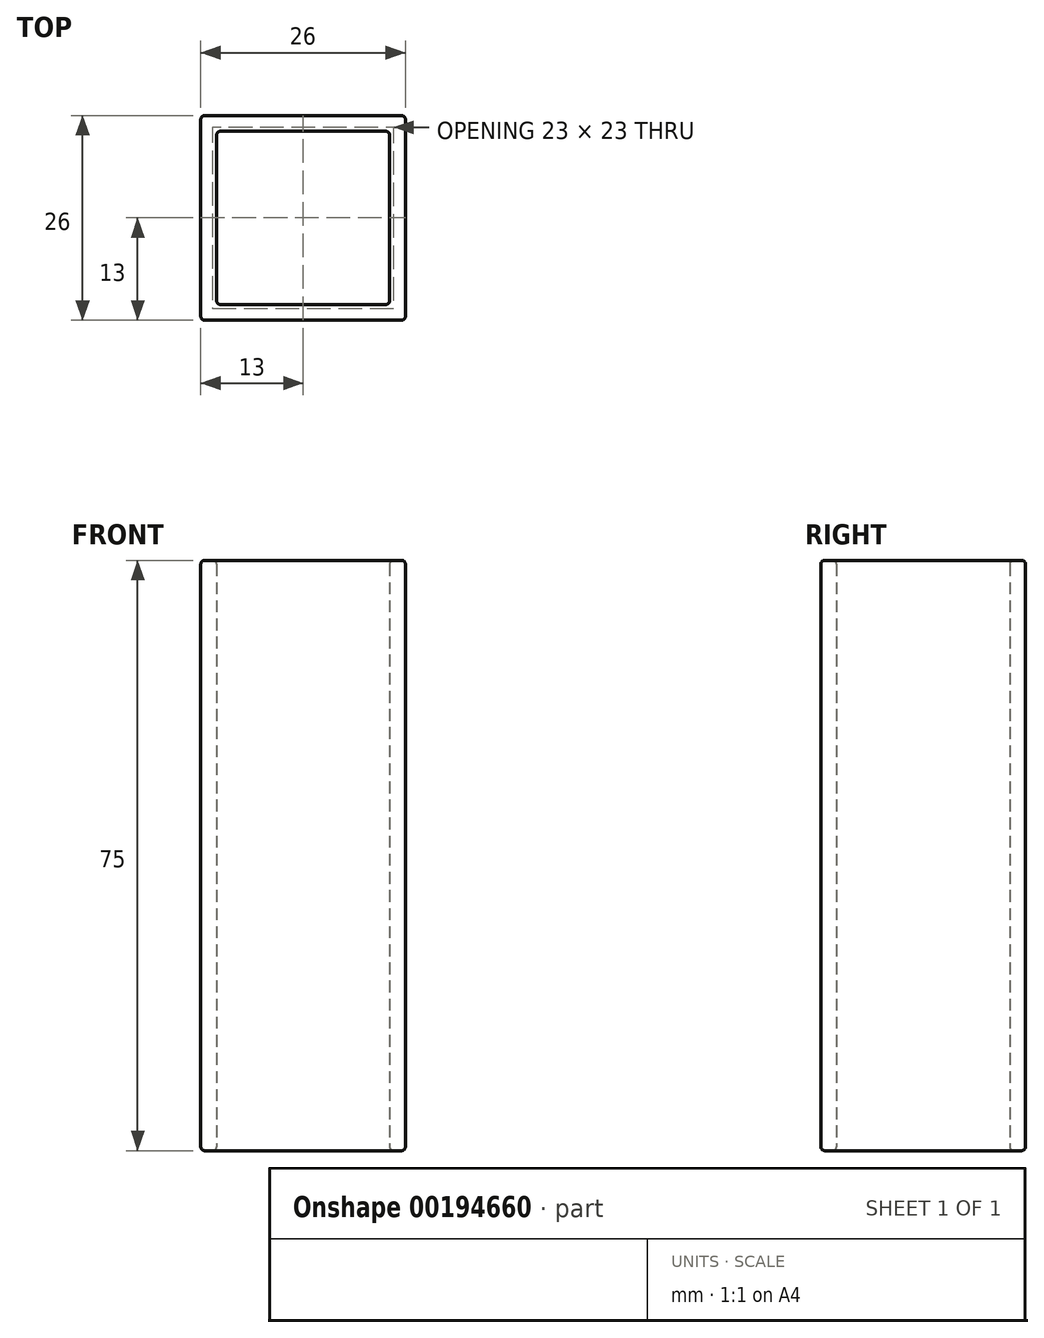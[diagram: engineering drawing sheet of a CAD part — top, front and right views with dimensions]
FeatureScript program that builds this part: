
annotation { "Feature Type Name" : "Feature", "Feature Type Description" : "" }
export const myFeature = defineFeature(function(context is Context, id is Id, definition is map)
    precondition{}
    {
        {
            var Q0;
            Q0=qCreatedBy(makeId("Top.planeOp"),FACE);
            var sketch = newSketch(context, id + "F0", { "sketchPlane" : qUnion([Q0])});
            skLineSegment(sketch, "E0.bottom", {"start": v(-13, 13) * mm, "end": v(13, 13) * mm});
            skLineSegment(sketch, "E0.top", {"start": v(-13, -13) * mm, "end": v(13, -13) * mm});
            skLineSegment(sketch, "E0.left", {"start": v(-13, 13) * mm, "end": v(-13, -13) * mm});
            skLineSegment(sketch, "E0.right", {"start": v(13, 13) * mm, "end": v(13, -13) * mm});
            skLineSegment(sketch, "E1.0", {"start": v(-11, 11) * mm, "end": v(11, 11) * mm});
            skLineSegment(sketch, "E1.1", {"start": v(-11, 11) * mm, "end": v(-11, -11) * mm});
            skLineSegment(sketch, "E1.2", {"start": v(-11, -11) * mm, "end": v(11, -11) * mm});
            skLineSegment(sketch, "E1.3", {"start": v(11, 11) * mm, "end": v(11, -11) * mm});
            skSolve(sketch);
        }
        {
            var Q0;
            Q0=makeQuery(id+"F0.imprint","IMPRINT",FACE,{"disambiguationData":[TD([[makeQuery(id+"F0.imprint","IMPRINT",EDGE,{"derivedFrom":sQuery(id+"F0.wireOp",EDGE,"E0.bottom")}),-1.0]])]});
            extrude(context, id + "F1", {"entities" : qUnion([Q0]), "depth" : 75 * mm});
        }
        {
            var Q0;
            Q0=makeQuery(id+"F1.opExtrude","SWEPT_FACE",FACE,{"disambiguationData":[OSD([sQuery(id+"F0.wireOp",EDGE,"E0.right")])]});
            var Q1;
            Q1=makeQuery(id+"F1.opExtrude","SWEPT_FACE",FACE,{"disambiguationData":[OSD([sQuery(id+"F0.wireOp",EDGE,"E0.bottom")])]});
            var Q2;
            Q2=makeQuery(id+"F1.opExtrude","SWEPT_FACE",FACE,{"disambiguationData":[OSD([sQuery(id+"F0.wireOp",EDGE,"E0.left")])]});
            var Q3;
            Q3=makeQuery(id+"F1.opExtrude","SWEPT_FACE",FACE,{"disambiguationData":[OSD([sQuery(id+"F0.wireOp",EDGE,"E0.top")])]});
            var Q4;
            Q4=makeQuery(id+"F1.opExtrude","SWEPT_FACE",FACE,{"disambiguationData":[OSD([sQuery(id+"F0.wireOp",EDGE,"E1.3")])]});
            var Q5;
            Q5=makeQuery(id+"F1.opExtrude","SWEPT_FACE",FACE,{"disambiguationData":[OSD([sQuery(id+"F0.wireOp",EDGE,"E1.2")])]});
            var Q6;
            Q6=makeQuery(id+"F1.opExtrude","SWEPT_FACE",FACE,{"disambiguationData":[OSD([sQuery(id+"F0.wireOp",EDGE,"E1.1")])]});
            var Q7;
            Q7=makeQuery(id+"F1.opExtrude","SWEPT_FACE",FACE,{"disambiguationData":[OSD([sQuery(id+"F0.wireOp",EDGE,"E1.0")])]});
            fillet(context, id + "F2", {"entities" : qUnion([Q0, Q1, Q2, Q3, Q4, Q5, Q6, Q7]), "radius" : 0.5 * mm, "tangentPropagation" : true, "allowEdgeOverflow" : false});
        }
    });
